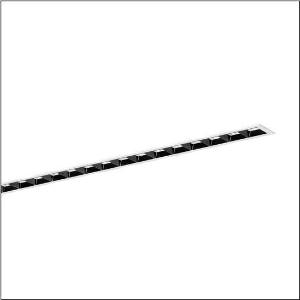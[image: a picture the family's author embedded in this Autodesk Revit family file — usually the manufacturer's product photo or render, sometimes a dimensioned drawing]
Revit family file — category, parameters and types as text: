
# Revit family: silica_r__21_51mx14tat4w_c2be
name_source: partatom
category: Lighting Fixtures
units: mm (PartAtom-declared; Revit-internal decimal feet)

## family parameters
Cut with Voids When Loaded = No
Host = Face
Light Source = No
Part Type = Normal
Room Calculation Point = No
Round Connector Dimension = Use Diameter
Shared = No

## types (1)
- --- (1 x LED, 3280 lm, 32.4 W, 6500K)
    Apparent Load = 32 VA
    CIE Flux Codes = 74 94 99 100 100
    Color Rendering = 80
    Color Temperature = 6500K
    Default Elevation = 1800 mm
    Description = Silica® 21, office luminaire, primary light control with darklight reflector, of PMMA, black, light emission: direct distribution, primary light characteristic: asymmetric, installation type: recessed, LED, rated luminous flux: 3.280lm, luminous efficacy: 96lm/W, light colour: 8tw, colour temperature: 2700..6500K, with terminal, 3+2-pole, max. 2.5mm², mains connection: 220..240V, AC, 50/60Hz, rated input power: 34.1W, luminaire housing, of aluminium, traffic white (RAL 9016), length: 1.228mm, width: 79mm, height: 53mm, protection rating (complete): IP20, insulation class (complete): insulation class I (protective earthing), certification: CE, permissible operating ambient temperature: 0..+35°C, standard: EN 50419, packaging unit: 1 piece
    Height = 0 mm  [stored 0 ft]
    Lamp = 1 x LED
    Lamp Light Flux = 3280 lm
    Lamp Power = 32.4 W
    Lamp count = 1
    Length = 1227 mm
    Luminous efficacy = 101 lm/W
    Manufacturer = Siteco
    ModVariant = No
    Model = 51MX14TAT4W
    Mounting Place = Ceiling
    Mounting Type = Recessed
    Number of Poles = 1
    OnlyDefault = Yes
    Power Factor = 1
    Product Name = Silica® 21
    Product group = office luminaire | ceiling recessed
    ProductGroupID = 401
    Protection Class = Protection class I
    Protection Degree = IP 20
    RLX_Detail_Level = 1
    RLX_Emergency_Light_Flux = 0 lm
    RLX_Emergency_Type = 0
    RLX_Emergency_Type_DB = No
    RlxData = <blob elided: 36297 chars, md5=35874759>
    Socket = socket
    Standby Power = 0 W
    System Light Flux = 3280 lm
    System Power = 32 W
    Type Comments = individual setting
    Type Image = l_1297791.jpg
    URL = http://relux.com
    VarID = @adj_071359
    Voltage = 0 V
    Weight = 0.00 kg
    Width = 79 mm

note: [stored X ft] marks values corroborated as IEEE doubles in the binary element streams (Revit-internal decimal feet)

## geometry (parser evidence)
native form markers: Blend x4, Sweep x10
no freeform markers — native parametric forms only
